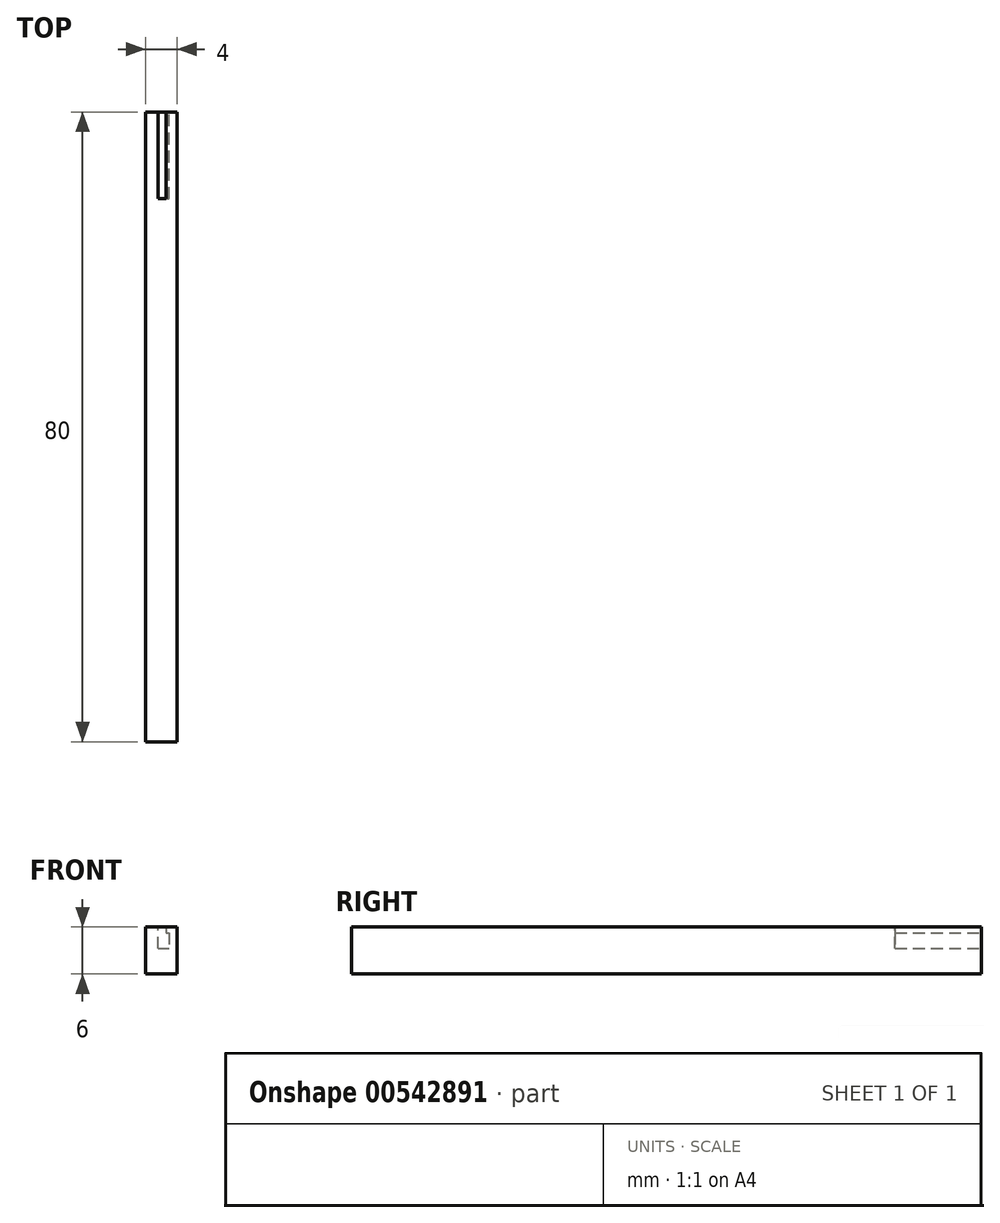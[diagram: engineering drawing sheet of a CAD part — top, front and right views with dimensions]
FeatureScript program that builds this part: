
annotation { "Feature Type Name" : "Feature", "Feature Type Description" : "" }
export const myFeature = defineFeature(function(context is Context, id is Id, definition is map)
    precondition{}
    {
        {
            var Q0;
            Q0=qCreatedBy(makeId("Top.planeOp"),FACE);
            var sketch = newSketch(context, id + "F0", { "sketchPlane" : qUnion([Q0])});
            skLineSegment(sketch, "E0.bottom", {"start": v(-4.45, 56.22) * mm, "end": v(-0.45, 56.22) * mm});
            skLineSegment(sketch, "E0.top", {"start": v(-4.45, -23.78) * mm, "end": v(-0.45, -23.78) * mm});
            skLineSegment(sketch, "E0.left", {"start": v(-4.45, 56.22) * mm, "end": v(-4.45, -23.78) * mm});
            skLineSegment(sketch, "E0.right", {"start": v(-0.45, 56.22) * mm, "end": v(-0.45, -23.78) * mm});
            skSolve(sketch);
        }
        {
            var Q0;
            Q0 = qSketchRegion(id + "F0", true);
            extrude(context, id + "F1", {"entities" : qUnion([Q0]), "depth" : 6 * mm, "offsetDistance" : 25 * mm});
        }
        {
            var Q0;
            Q0=makeQuery(id+"F1.opExtrude","SWEPT_FACE",FACE,{"disambiguationData":[OSD([sQuery(id+"F0.wireOp",EDGE,"E0.bottom")])]});
            var sketch = newSketch(context, id + "F2", { "sketchPlane" : qUnion([Q0])});
            skLineSegment(sketch, "E1", {"start": v(1.85, 6) * mm, "end": v(1.85, 5.25) * mm});
            skLineSegment(sketch, "E2", {"start": v(2.85, 6) * mm, "end": v(1.85, 6) * mm});
            skLineSegment(sketch, "E3", {"start": v(1.85, 5.25) * mm, "end": v(1.45, 5.25) * mm});
            skLineSegment(sketch, "E4", {"start": v(1.45, 5.25) * mm, "end": v(1.45, 3.25) * mm});
            skLineSegment(sketch, "E5", {"start": v(2.85, 3.25) * mm, "end": v(1.45, 3.25) * mm});
            skLineSegment(sketch, "E6", {"start": v(2.85, 3.25) * mm, "end": v(2.85, 6) * mm});
            skSolve(sketch);
        }
        {
            var Q0;
            Q0=makeQuery(id+"F2.imprint","IMPRINT",FACE,{"disambiguationData":[TD([[makeQuery(id+"F2.imprint","IMPRINT",EDGE,{"derivedFrom":sQuery(id+"F2.wireOp",EDGE,"E1")}),1.0]])]});
            extrude(context, id + "F3", {"entities" : qUnion([Q0]), "operationType" : NewBodyOperationType.REMOVE, "oppositeDirection" : true, "depth" : 11 * mm, "offsetDistance" : 25 * mm});
        }
    });
